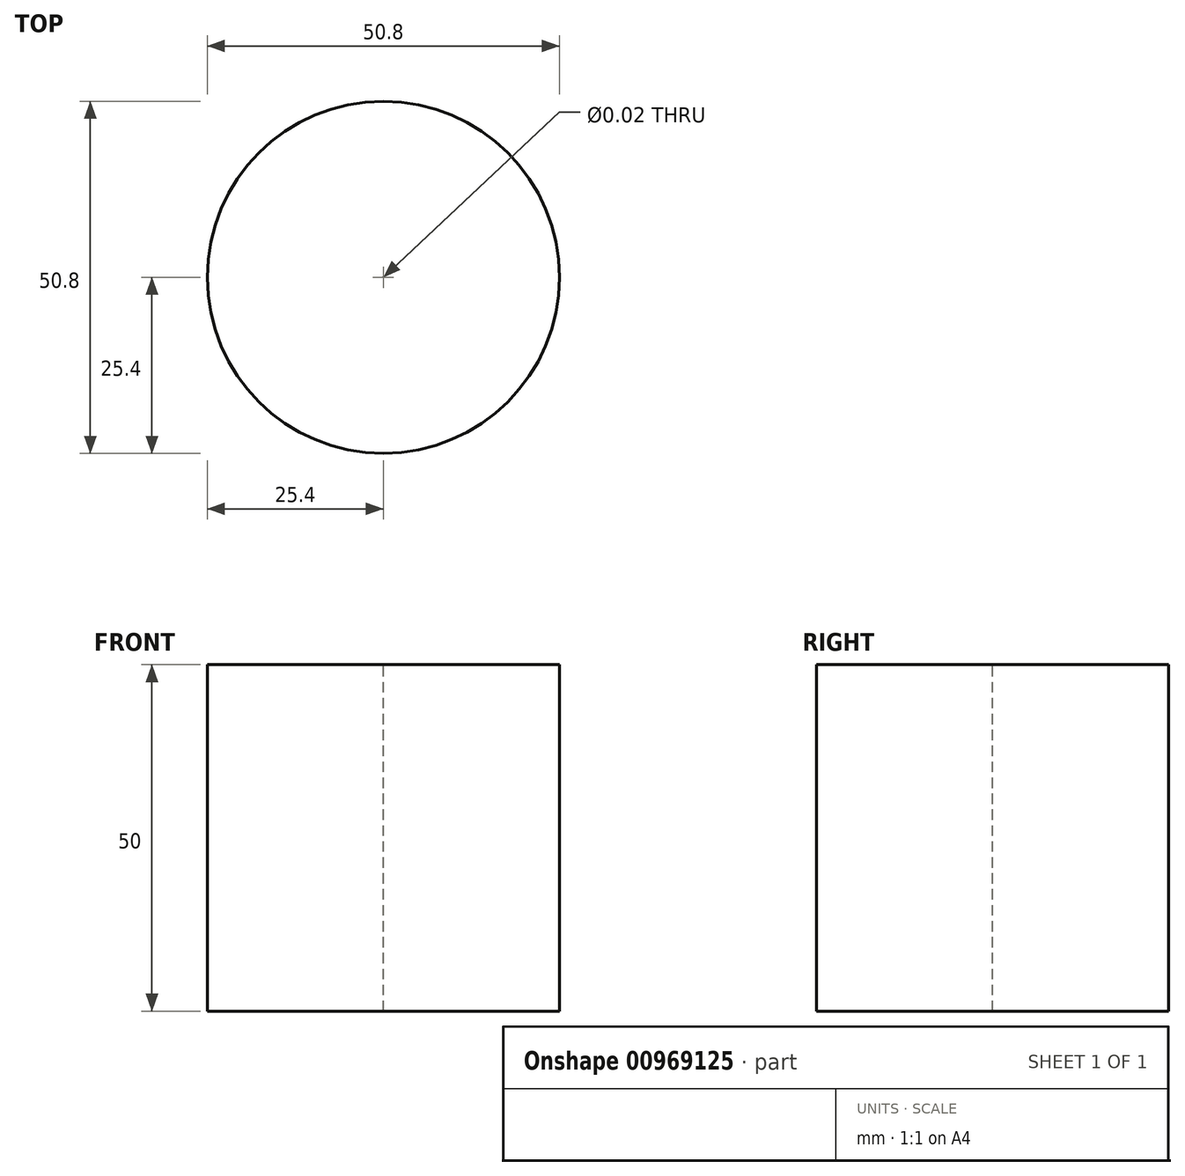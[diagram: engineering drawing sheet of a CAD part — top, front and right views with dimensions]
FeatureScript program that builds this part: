
annotation { "Feature Type Name" : "Feature", "Feature Type Description" : "" }
export const myFeature = defineFeature(function(context is Context, id is Id, definition is map)
    precondition{}
    {
        {
            var Q0;
            Q0=qCreatedBy(makeId("Top.planeOp"),FACE);
            var sketch = newSketch(context, id + "F0", { "sketchPlane" : qUnion([Q0])});
            skCircle(sketch, "E0", {"center": v(0, 0) * mm, "radius": 25.4 * mm});
            skSolve(sketch);
        }
        {
            var Q0;
            Q0 = qSketchRegion(id + "F0", true);
            extrude(context, id + "F1", {"entities" : qUnion([Q0]), "depth" : 50 * mm, "offsetDistance" : 25.4 * mm});
        }
        {
            var Q0;
            Q0=makeQuery(id+"F1.opExtrude","CAP_FACE",FACE,{"disambiguationData":[OSD([sQuery(id+"F0.wireOp",EDGE,"E0")])],"isStart":false});
            var sketch = newSketch(context, id + "F2", { "sketchPlane" : qUnion([Q0])});
            skPoint(sketch, "E1", {"position": v(0, 0) * mm});
            skSolve(sketch);
        }
        {
            var Q0;
            Q0=sQuery(id+"F2.wireOp",VERTEX,"E1");
            var Q1;
            Q1=makeQuery(id+"F1.opExtrude","SWEPT_BODY",BODY,{"disambiguationData":[OSD([sQuery(id+"F0.wireOp",EDGE,"E0")])]});
            hole(context, id + "F3", {"style" : HoleStyle.SIMPLE, "endStyle" : HoleEndStyle.THROUGH, "standardTappedOrClearance" : lookupTablePath({ "standard" : "ANSI", "size" : "1/2 (0.5)", "type" : "Drilled" }), "standardBlindInLast" : lookupTablePath({ "standard" : "ANSI", "size" : "1/2 (0.5)", "type" : "Drilled" }), "holeDiameter" : 1 / 50.8 * mm, "majorDiameter" : 6.35 * mm, "isTappedThrough" : true, "tappedDepth" : 12.7 * mm, "tapClearance" : 3, "locations" : qUnion([Q0]), "scope" : qUnion([Q1])});
        }
    });
